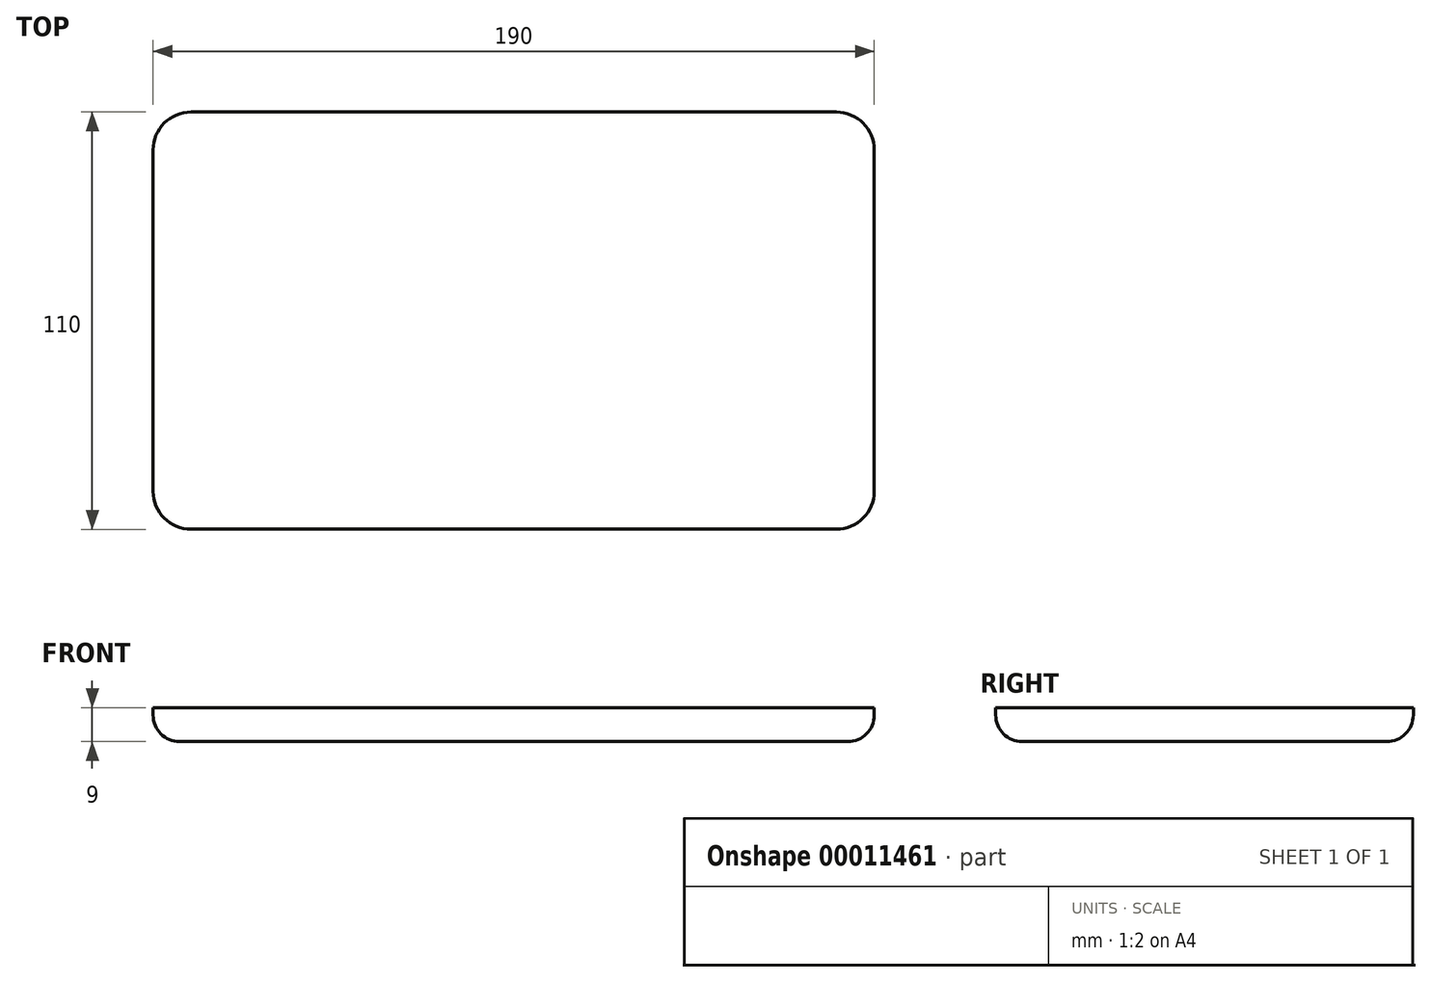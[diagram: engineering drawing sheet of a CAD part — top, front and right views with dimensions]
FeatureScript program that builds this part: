
annotation { "Feature Type Name" : "Feature", "Feature Type Description" : "" }
export const myFeature = defineFeature(function(context is Context, id is Id, definition is map)
    precondition{}
    {
        {
            var Q0;
            Q0=qCreatedBy(makeId("Top.planeOp"),FACE);
            var sketch = newSketch(context, id + "F0", { "sketchPlane" : qUnion([Q0])});
            skLineSegment(sketch, "E0.bottom", {"start": v(-86.3, 53.8) * mm, "end": v(83.7, 53.8) * mm});
            skLineSegment(sketch, "E0.top", {"start": v(-86.3, -56.2) * mm, "end": v(83.7, -56.2) * mm});
            skLineSegment(sketch, "E0.left", {"start": v(-96.3, 43.8) * mm, "end": v(-96.3, -46.2) * mm});
            skLineSegment(sketch, "E0.right", {"start": v(93.7, 43.8) * mm, "end": v(93.7, -46.2) * mm});
            skPoint(sketch, "E1.visualSharp", {"position": v(-96.3, 53.8) * mm});
            skArc(sketch, "E1.filletArc", {"start": v(-86.3, 53.8) * mm, "mid": v(-93.38, 50.86) * mm, "end": v(-96.3, 43.8) * mm});
            skPoint(sketch, "E2.visualSharp", {"position": v(93.7, 53.8) * mm});
            skArc(sketch, "E2.filletArc", {"start": v(93.7, 43.8) * mm, "mid": v(90.76, 50.86) * mm, "end": v(83.7, 53.8) * mm});
            skPoint(sketch, "E3.visualSharp", {"position": v(93.7, -56.2) * mm});
            skArc(sketch, "E3.filletArc", {"start": v(83.7, -56.2) * mm, "mid": v(90.76, -53.28) * mm, "end": v(93.7, -46.2) * mm});
            skPoint(sketch, "E4.visualSharp", {"position": v(-96.3, -56.2) * mm});
            skArc(sketch, "E4.filletArc", {"start": v(-96.3, -46.2) * mm, "mid": v(-93.38, -53.28) * mm, "end": v(-86.3, -56.2) * mm});
            skSolve(sketch);
        }
        {
            var Q0;
            Q0 = qSketchRegion(id + "F0", true);
            extrude(context, id + "F1", {"entities" : qUnion([Q0]), "depth" : 9 * mm});
        }
        {
            var Q0;
            Q0=makeQuery(id+"F1.opExtrude","CAP_FACE",FACE,{"disambiguationData":[OSD([sQuery(id+"F0.wireOp",EDGE,"E0.bottom"),sQuery(id+"F0.wireOp",EDGE,"E0.top"),sQuery(id+"F0.wireOp",EDGE,"E0.left"),sQuery(id+"F0.wireOp",EDGE,"E0.right"),sQuery(id+"F0.wireOp",EDGE,"E1.filletArc"),sQuery(id+"F0.wireOp",EDGE,"E2.filletArc"),sQuery(id+"F0.wireOp",EDGE,"E3.filletArc"),sQuery(id+"F0.wireOp",EDGE,"E4.filletArc")])],"isStart":true});
            fillet(context, id + "F2", {"entities" : qUnion([Q0]), "radius" : 7 * mm, "allowEdgeOverflow" : false});
        }
    });
